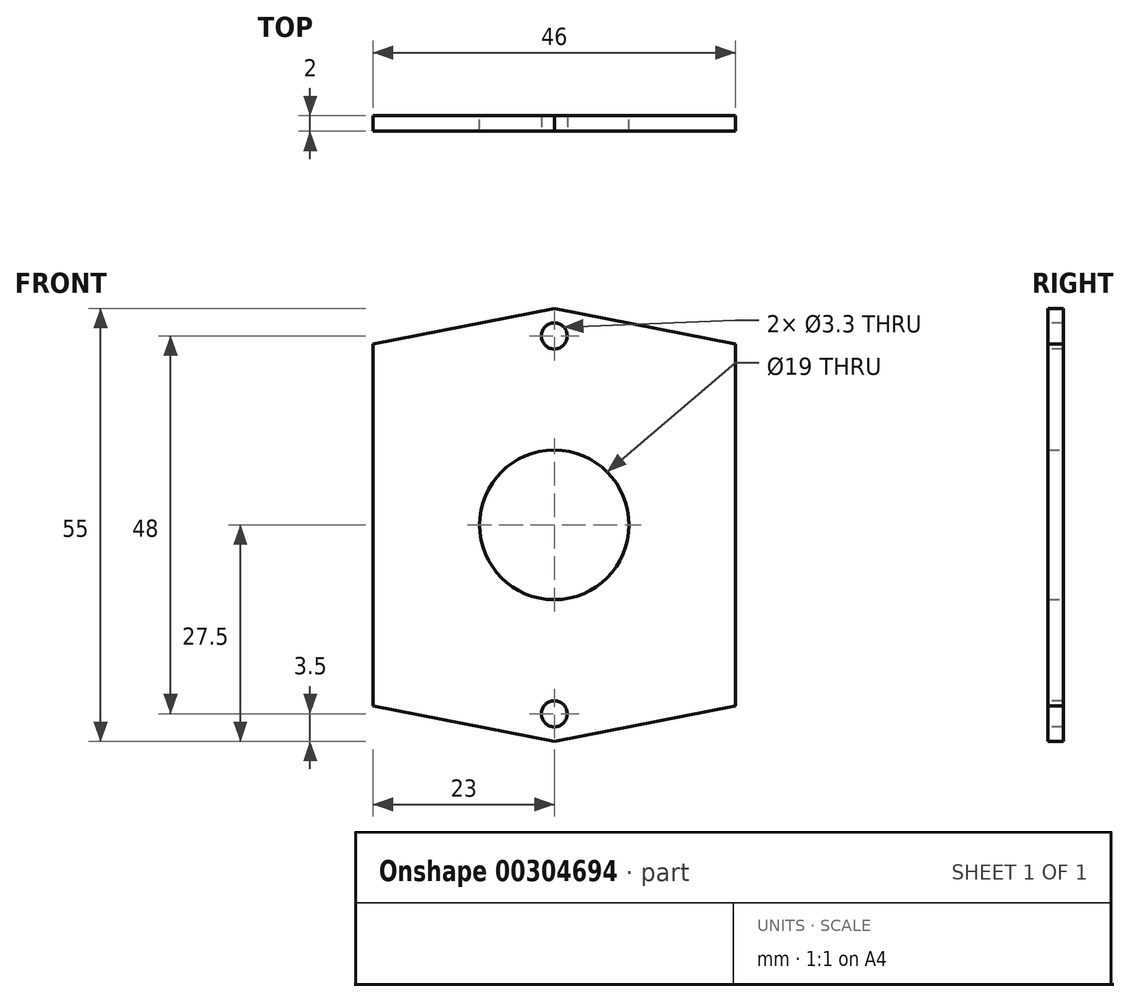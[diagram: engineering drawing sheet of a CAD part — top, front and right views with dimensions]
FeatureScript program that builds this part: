
annotation { "Feature Type Name" : "Feature", "Feature Type Description" : "" }
export const myFeature = defineFeature(function(context is Context, id is Id, definition is map)
    precondition{}
    {
        {
            var Q0;
            Q0=qCreatedBy(makeId("Front.planeOp"),FACE);
            var sketch = newSketch(context, id + "F0", { "sketchPlane" : qUnion([Q0])});
            skLineSegment(sketch, "E0.bottom", {"start": v(23, 23) * mm, "end": v(-23, 23) * mm});
            skLineSegment(sketch, "E0.top", {"start": v(23, -23) * mm, "end": v(-23, -23) * mm});
            skLineSegment(sketch, "E0.left", {"start": v(23, 23) * mm, "end": v(23, -23) * mm});
            skLineSegment(sketch, "E0.right", {"start": v(-23, 23) * mm, "end": v(-23, -23) * mm});
            skPoint(sketch, "E0.middle", {"position": v(0, 0) * mm});
            skLineSegment(sketch, "E1", {"start": v(-23, 23) * mm, "end": v(0, 27.5) * mm});
            skLineSegment(sketch, "E2", {"start": v(0, 27.5) * mm, "end": v(23, 23) * mm});
            skLineSegment(sketch, "E3", {"start": v(-23, -23) * mm, "end": v(0, -27.5) * mm});
            skLineSegment(sketch, "E4", {"start": v(0, -27.5) * mm, "end": v(23, -23) * mm});
            skLineSegment(sketch, "E5.left", {"start": v(23, -23) * mm, "end": v(23, -19) * mm});
            skSolve(sketch);
        }
        {
            var Q0;
            Q0 = qSketchRegion(id + "F0", true);
            extrude(context, id + "F1", {"entities" : qUnion([Q0]), "offsetDistance" : 25 * mm, "depth" : 2 * mm});
        }
        {
            var Q0;
            Q0=makeQuery(id+"F1.opExtrude","CAP_FACE",FACE,{"disambiguationData":[OSD([sQuery(id+"F0.wireOp",EDGE,"E0.left"),sQuery(id+"F0.wireOp",EDGE,"E0.right"),sQuery(id+"F0.wireOp",EDGE,"E1"),sQuery(id+"F0.wireOp",EDGE,"E2"),sQuery(id+"F0.wireOp",EDGE,"E3"),sQuery(id+"F0.wireOp",EDGE,"E4")])],"isStart":true});
            var sketch = newSketch(context, id + "F2", { "sketchPlane" : qUnion([Q0])});
            skCircle(sketch, "E6", {"center": v(0, 0) * mm, "radius": 9.5 * mm});
            skSolve(sketch);
        }
        {
            var Q0;
            Q0 = qSketchRegion(id + "F2", true);
            extrude(context, id + "F3", {"entities" : qUnion([Q0]), "operationType" : NewBodyOperationType.REMOVE, "oppositeDirection" : true, "depth" : 25 * mm});
        }
        {
            var Q0;
            Q0=makeQuery(id+"F1.opExtrude","CAP_FACE",FACE,{"disambiguationData":[OSD([sQuery(id+"F0.wireOp",EDGE,"E0.left"),sQuery(id+"F0.wireOp",EDGE,"E0.right"),sQuery(id+"F0.wireOp",EDGE,"E1"),sQuery(id+"F0.wireOp",EDGE,"E2"),sQuery(id+"F0.wireOp",EDGE,"E3"),sQuery(id+"F0.wireOp",EDGE,"E4")])],"isStart":true});
            var sketch = newSketch(context, id + "F4", { "sketchPlane" : qUnion([Q0])});
            skLineSegment(sketch, "E7", {"start": v(23, 0) * mm, "end": v(-23, 0) * mm, "construction": true});
            skSolve(sketch);
        }
        {
            var Q0;
            Q0=makeQuery(id+"F1.opExtrude","CAP_FACE",FACE,{"disambiguationData":[OSD([sQuery(id+"F0.wireOp",EDGE,"E0.left"),sQuery(id+"F0.wireOp",EDGE,"E0.right"),sQuery(id+"F0.wireOp",EDGE,"E1"),sQuery(id+"F0.wireOp",EDGE,"E2"),sQuery(id+"F0.wireOp",EDGE,"E3"),sQuery(id+"F0.wireOp",EDGE,"E4")])],"isStart":false});
            var sketch = newSketch(context, id + "F5", { "sketchPlane" : qUnion([Q0])});
            skLineSegment(sketch, "E8", {"start": v(0, 27.5) * mm, "end": v(0, -27.5) * mm, "construction": true});
            skPoint(sketch, "E9.endSnap0", {"position": v(-11.5, 25.25) * mm});
            skLineSegment(sketch, "E10", {"start": v(-23, 0) * mm, "end": v(23, 0) * mm, "construction": true});
            skLineSegment(sketch, "E11", {"start": v(-23, 24) * mm, "end": v(23, 24) * mm, "construction": true});
            skLineSegment(sketch, "E12", {"start": v(-23, -24) * mm, "end": v(23, -24) * mm, "construction": true});
            skPoint(sketch, "E13", {"position": v(0, 24) * mm});
            skPoint(sketch, "E14", {"position": v(0, -24) * mm});
            skSolve(sketch);
        }
        {
            var Q0;
            Q0=sQuery(id+"F5.wireOp",VERTEX,"E14");
            var Q1;
            Q1=sQuery(id+"F5.wireOp",VERTEX,"E13");
            var Q2;
            Q2=makeQuery(id+"F1.opExtrude","SWEPT_BODY",BODY,{"disambiguationData":[OSD([sQuery(id+"F0.wireOp",EDGE,"E0.left"),sQuery(id+"F0.wireOp",EDGE,"E0.right"),sQuery(id+"F0.wireOp",EDGE,"E1"),sQuery(id+"F0.wireOp",EDGE,"E2"),sQuery(id+"F0.wireOp",EDGE,"E3"),sQuery(id+"F0.wireOp",EDGE,"E4")])]});
            hole(context, id + "F6", {"style" : HoleStyle.SIMPLE, "endStyle" : HoleEndStyle.THROUGH, "standardTappedOrClearance" : lookupTablePath({ "standard" : "ISO", "fit" : "Normal", "size" : "M3", "type" : "Clearance" }), "standardBlindInLast" : lookupTablePath({ "fit" : "Standard", "standard" : "ISO", "size" : "M3", "type" : "Clearance" }), "holeDiameter" : 3.3 * mm, "tappedDepth" : 12 * mm, "tapClearance" : 3, "locations" : qUnion([Q0, Q1]), "scope" : qUnion([Q2])});
        }
    });
